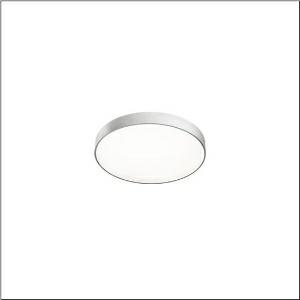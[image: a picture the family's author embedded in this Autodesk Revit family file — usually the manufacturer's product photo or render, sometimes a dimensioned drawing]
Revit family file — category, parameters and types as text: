
# Revit family: round_21_s_51mr34fd0321s
name_source: partatom
category: Lighting Fixtures
units: mm (PartAtom-declared; Revit-internal decimal feet)

## family parameters
Cut with Voids When Loaded = No
Host = Face
Light Source = No
Part Type = Normal
Room Calculation Point = No
Round Connector Dimension = Use Diameter
Shared = No

## types (1)
- Round 21 S (1 x LED, 3750 lm, 30.3 W, 3000K)
    Apparent Load = 30 VA
    CIE Flux Codes = 49 80 96 100 100
    Color Rendering = 80
    Color Temperature = 3000K
    Default Elevation = 1800 mm
    Description = Round 21 S, wall and ceiling luminaire, primary optical cover: cover, of PMMA, opal, light emission: direct distribution, primary light characteristic: symmetric, installation type: suspended mounting, surface-mounted, LED, rated luminous flux: 3.750lm, luminous efficacy: 124lm/W, light colour: 830, colour temperature: 3000K, control gear: DALI 2, with terminal, 5-pole, mains connection: 230V, AC, 50/60Hz, rated input power: 30.3W, housing, of aluminium, coated, silver, diameter: 400mm, height: 62mm, protection rating (complete): IP40, insulation class (complete): insulation class I (protective earthing), certification: CE, impact resistance: IK04, permissible operating ambient temperature: -10..+35°C, packaging unit: 1 piece
    Height = 87 mm
    Lamp = 1 x LED
    Lamp Light Flux = 3750 lm
    Lamp Power = 30.3 W
    Lamp count = 1
    Length = 400 mm
    Luminous efficacy = 124 lm/W
    Manufacturer = Siteco
    ModVariant = No
    Model = 51MR34FD0321S
    Mounting Place = Ceiling
    Mounting Type = Surface mounted
    Number of Poles = 1
    OnlyDefault = Yes
    Power Factor = 1
    Product Name = Round 21 S
    Product group = wall and ceiling luminaire
    ProductGroupID = 304
    Protection Class = Protection class I
    Protection Degree = IP 40
    RLX_Detail_Level = 1
    RLX_Emergency_Light_Flux = 0 lm
    RLX_Emergency_Type = 0
    RLX_Emergency_Type_DB = No
    RlxData = <blob elided: 11157 chars, md5=abc9c244>
    Socket = socket
    Standby Power = 0 W
    System Light Flux = 3750 lm
    System Power = 30 W
    Type Comments = Product without accessories
    Type Image = l_1258309.jpg
    URL = http://relux.com
    VarID = ---
    Voltage = 0 V
    Weight = 0.00 kg
    Width = 0 mm  [stored 0 ft]

note: [stored X ft] marks values corroborated as IEEE doubles in the binary element streams (Revit-internal decimal feet)

## geometry (parser evidence)
native form markers: Sweep x8
no freeform markers — native parametric forms only
